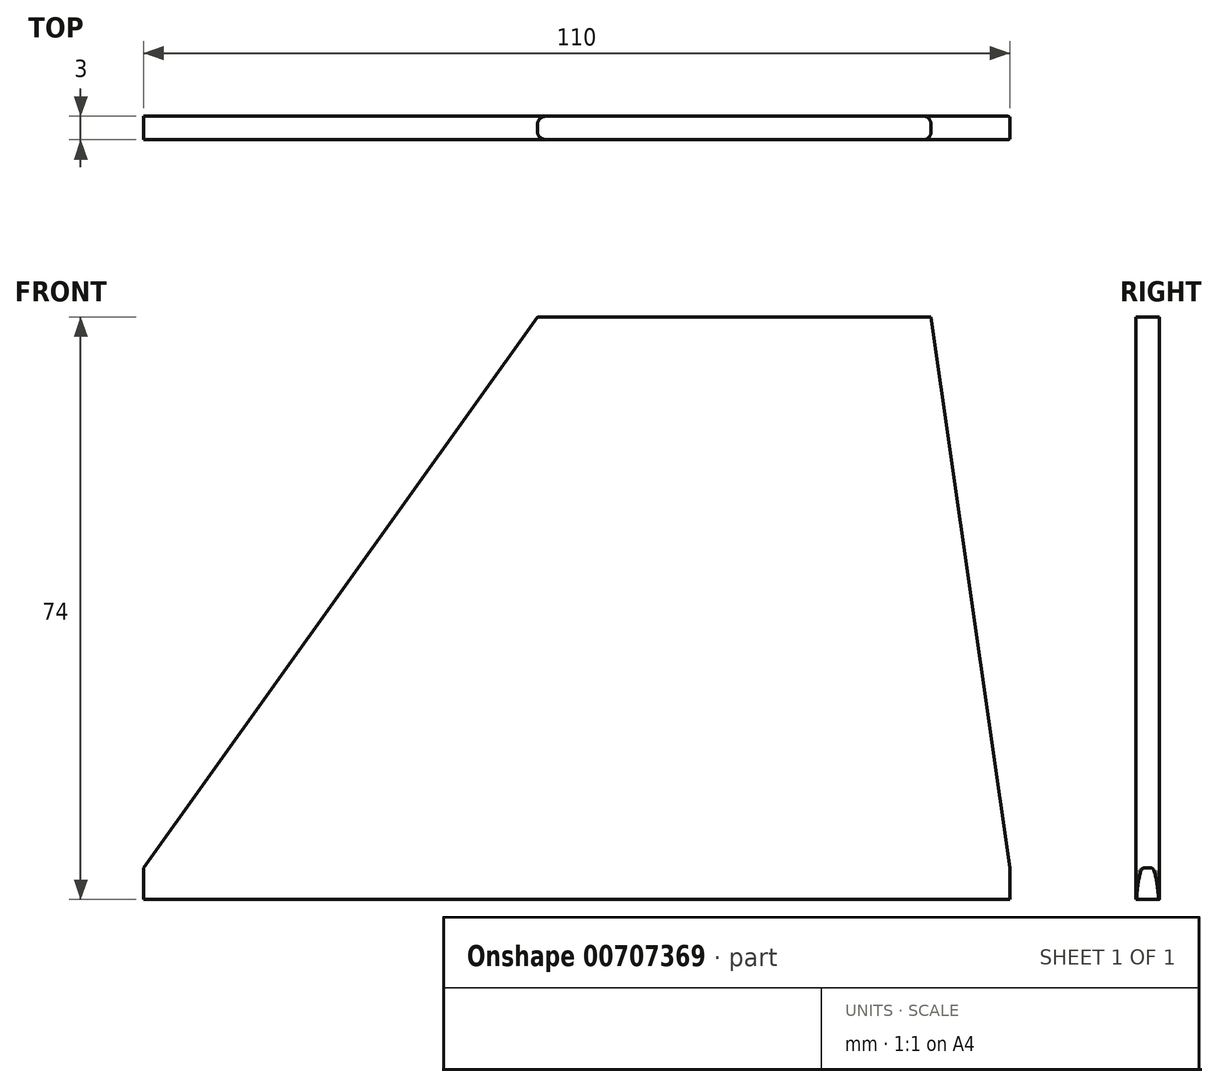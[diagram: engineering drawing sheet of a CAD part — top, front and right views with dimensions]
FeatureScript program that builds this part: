
annotation { "Feature Type Name" : "Feature", "Feature Type Description" : "" }
export const myFeature = defineFeature(function(context is Context, id is Id, definition is map)
    precondition{}
    {
        {
            var Q0;
            Q0=qCreatedBy(makeId("Front.planeOp"),FACE);
            var sketch = newSketch(context, id + "F0", { "sketchPlane" : qUnion([Q0])});
            skLineSegment(sketch, "E0", {"start": v(-50, 0) * mm, "end": v(60, 0) * mm});
            skLineSegment(sketch, "E1", {"start": v(60, 0) * mm, "end": v(50, 70) * mm});
            skLineSegment(sketch, "E2", {"start": v(50, 70) * mm, "end": v(0, 70) * mm});
            skLineSegment(sketch, "E3", {"start": v(0, 70) * mm, "end": v(-50, 0) * mm});
            skLineSegment(sketch, "E4", {"start": v(-50, 0) * mm, "end": v(-50, -4) * mm});
            skLineSegment(sketch, "E5", {"start": v(-50, -4) * mm, "end": v(60, -4) * mm});
            skLineSegment(sketch, "E6", {"start": v(60, -4) * mm, "end": v(60, 0) * mm});
            skSolve(sketch);
        }
        {
            var Q0;
            Q0=makeQuery(id+"F0.imprint","IMPRINT",FACE,{"disambiguationData":[TD([[makeQuery(id+"F0.imprint","IMPRINT",EDGE,{"derivedFrom":sQuery(id+"F0.wireOp",EDGE,"E0")}),1.0]])]});
            var Q1;
            Q1=makeQuery(id+"F0.imprint","IMPRINT",FACE,{"disambiguationData":[TD([[makeQuery(id+"F0.imprint","IMPRINT",EDGE,{"derivedFrom":sQuery(id+"F0.wireOp",EDGE,"E0")}),-1.0]])]});
            extrude(context, id + "F1", {"entities" : qUnion([Q0, Q1]), "depth" : 3 * mm, "offsetDistance" : 25 * mm});
        }
        {
            var Q0;
            Q0=makeQuery(id+"F1.opExtrude","CAP_EDGE",EDGE,{"disambiguationData":[OSD([sQuery(id+"F0.wireOp",EDGE,"E3")])],"isStart":false});
            var Q1;
            Q1=makeQuery(id+"F1.opExtrude","CAP_EDGE",EDGE,{"disambiguationData":[OSD([sQuery(id+"F0.wireOp",EDGE,"E3")])],"isStart":true});
            var Q2;
            Q2=makeQuery(id+"F1.opExtrude","CAP_EDGE",EDGE,{"disambiguationData":[OSD([sQuery(id+"F0.wireOp",EDGE,"E1")])],"isStart":false});
            var Q3;
            Q3=makeQuery(id+"F1.opExtrude","CAP_EDGE",EDGE,{"disambiguationData":[OSD([sQuery(id+"F0.wireOp",EDGE,"E1")])],"isStart":true});
            fillet(context, id + "F2", {"entities" : qUnion([Q0, Q1, Q2, Q3]), "radius" : 1 * mm, "tangentPropagation" : true, "allowEdgeOverflow" : false});
        }
    });
